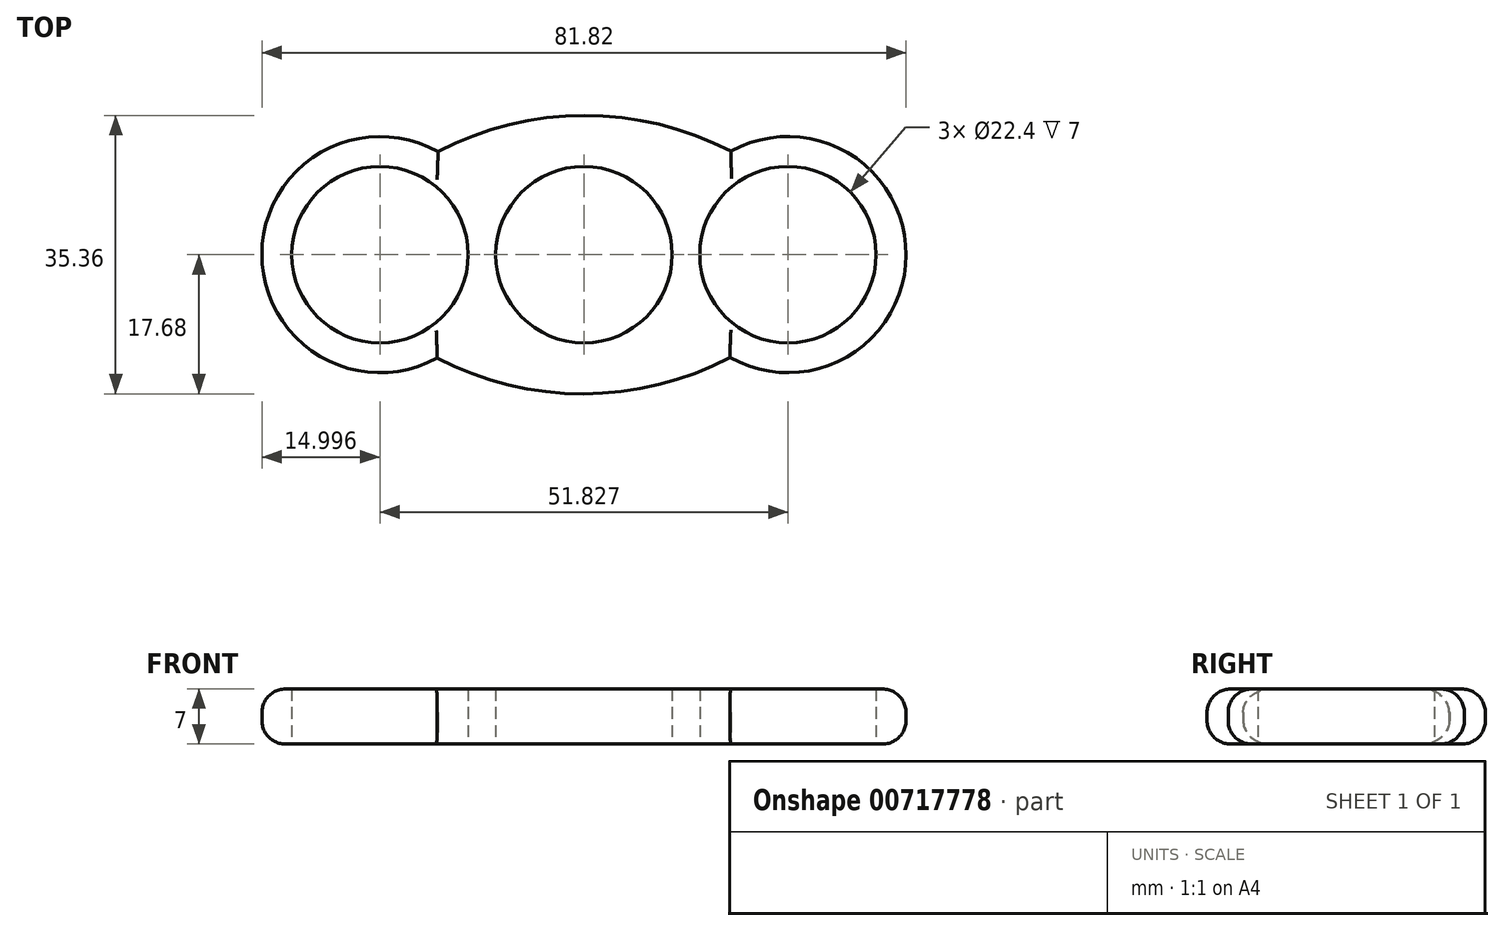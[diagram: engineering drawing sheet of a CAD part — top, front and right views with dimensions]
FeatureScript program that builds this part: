
annotation { "Feature Type Name" : "Feature", "Feature Type Description" : "" }
export const myFeature = defineFeature(function(context is Context, id is Id, definition is map)
    precondition{}
    {
        {
            var Q0;
            Q0=qCreatedBy(makeId("Top.planeOp"),FACE);
            var sketch = newSketch(context, id + "F0", { "sketchPlane" : qUnion([Q0])});
            skCircle(sketch, "E0", {"center": v(0, 0) * mm, "radius": 11.2 * mm});
            skCircle(sketch, "E1", {"center": v(-25.91, 0) * mm, "radius": 11.2 * mm});
            skArc(sketch, "E2", {"start": v(-18.54, 13.06) * mm, "mid": v(-40.91, 0.07) * mm, "end": v(-18.66, -13.13) * mm});
            skLineSegment(sketch, "E3.anchor1", {"start": v(0, 0) * mm, "end": v(-25.91, 0) * mm, "construction": true});
            skLineSegment(sketch, "E3.anchor2", {"start": v(-25.91, 0) * mm, "end": v(0, 0) * mm, "construction": true});
            skArc(sketch, "E4", {"start": v(-18.66, -13.13) * mm, "mid": v(-0.05, -17.68) * mm, "end": v(18.54, -13.06) * mm});
            skArc(sketch, "E5.1.0", {"start": v(18.66, 13.13) * mm, "mid": v(0.05, 17.68) * mm, "end": v(-18.54, 13.06) * mm});
            skArc(sketch, "E6.trimOffspring", {"start": v(18.54, -13.06) * mm, "mid": v(40.91, -0.07) * mm, "end": v(18.66, 13.13) * mm});
            skCircle(sketch, "E7", {"center": v(25.91, 0) * mm, "radius": 11.2 * mm});
            skSolve(sketch);
        }
        {
            var Q0;
            Q0=makeQuery(id+"F0.imprint","IMPRINT",FACE,{"disambiguationData":[TD([[makeQuery(id+"F0.imprint","IMPRINT",EDGE,{"derivedFrom":sQuery(id+"F0.wireOp",EDGE,"E2")}),1.0]])]});
            extrude(context, id + "F1", {"entities" : qUnion([Q0]), "depth" : 7 * mm, "offsetDistance" : 25 * mm});
        }
        {
            var Q0;
            Q0=makeQuery(id+"F1.opExtrude","CAP_EDGE",EDGE,{"disambiguationData":[OSD([sQuery(id+"F0.wireOp",EDGE,"E5.1.0")])],"isStart":false});
            var Q1;
            Q1=makeQuery(id+"F1.opExtrude","CAP_EDGE",EDGE,{"disambiguationData":[OSD([sQuery(id+"F0.wireOp",EDGE,"E6.trimOffspring")])],"isStart":false});
            var Q2;
            Q2=makeQuery(id+"F1.opExtrude","CAP_EDGE",EDGE,{"disambiguationData":[OSD([sQuery(id+"F0.wireOp",EDGE,"E4")])],"isStart":false});
            var Q3;
            Q3=makeQuery(id+"F1.opExtrude","CAP_EDGE",EDGE,{"disambiguationData":[OSD([sQuery(id+"F0.wireOp",EDGE,"E2")])],"isStart":true});
            var Q4;
            Q4=makeQuery(id+"F1.opExtrude","CAP_EDGE",EDGE,{"disambiguationData":[OSD([sQuery(id+"F0.wireOp",EDGE,"E5.1.0")])],"isStart":true});
            var Q5;
            Q5=makeQuery(id+"F1.opExtrude","CAP_EDGE",EDGE,{"disambiguationData":[OSD([sQuery(id+"F0.wireOp",EDGE,"E6.trimOffspring")])],"isStart":true});
            var Q6;
            Q6=makeQuery(id+"F1.opExtrude","CAP_EDGE",EDGE,{"disambiguationData":[OSD([sQuery(id+"F0.wireOp",EDGE,"E4")])],"isStart":true});
            var Q7;
            Q7=makeQuery(id+"F1.opExtrude","CAP_EDGE",EDGE,{"disambiguationData":[OSD([sQuery(id+"F0.wireOp",EDGE,"E2")])],"isStart":false});
            fillet(context, id + "F2", {"entities" : qUnion([Q0, Q1, Q2, Q3, Q4, Q5, Q6, Q7]), "radius" : 3 * mm, "allowEdgeOverflow" : false});
        }
    });
